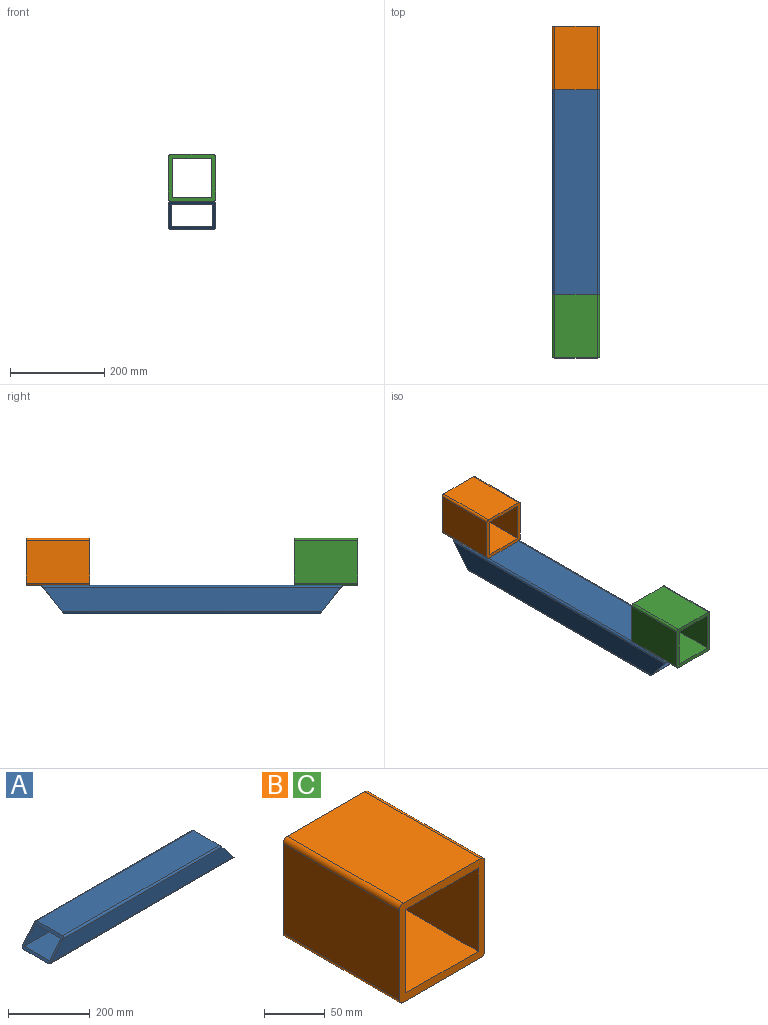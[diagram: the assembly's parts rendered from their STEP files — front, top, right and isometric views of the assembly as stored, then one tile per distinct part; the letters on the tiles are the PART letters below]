
ASSEMBLY  parts=3 mates=2
PART A: 14 faces, bbox 640x100x60 mm
  f0: cylinder r=5mm len=550.92mm, axis (-1,0,0), area 4286.5mm2, adj f1,f11,f12,f13
  f1: plane 631.9x50mm, normal (0,-1,0), area 29570.6mm2, adj f0,f2,f12,f13
  f2: cylinder r=5mm len=640mm, axis (-1,0,0), area 5003.4mm2, adj f1,f3,f12,f13
  f3: plane 640x90mm, normal (0,0,-1), area 57600mm2, adj f2,f4,f12,f13
  f4: cylinder r=5mm len=640mm, axis (-1,0,0), area 5003.4mm2, adj f3,f5,f12,f13
  f5: plane 631.9x50mm, normal (0,1,0), area 29570.6mm2, adj f4,f6,f12,f13
  f6: cylinder r=5mm len=550.92mm, axis (-1,0,0), area 4286.5mm2, adj f5,f11,f12,f13
  f7: plane 630.28x48mm, normal (0,1,0), area 28387.8mm2, adj f8,f10,f12,f13
  f8: plane 552.54x88mm, normal (0,0,-1), area 48623.8mm2, adj f7,f9,f12,f13
  f9: plane 630.28x48mm, normal (0,-1,0), area 28387.8mm2, adj f8,f10,f12,f13
  f10: plane 630.28x88mm, normal (0,0,1), area 55464.9mm2, adj f7,f9,f12,f13
  f11: plane 542.83x90mm, normal (0,0,1), area 48854.3mm2, adj f0,f6,f12,f13
  f12: plane 100x60mm, normal (-0.78,0,0.63), area 2257.7mm2, adj f0,f1,f2,f3,f4,f5,f6,f7
  f13: plane 100x60mm, normal (0.78,0,0.63), area 2257.7mm2, adj f0,f1,f2,f3,f4,f5,f6,f7
PART B: 14 faces, bbox 100x135x100 mm
  f0: cylinder r=5mm len=135mm, axis (0,1,0), area 1060.3mm2, adj f1,f11,f12,f13
  f1: plane 135x90mm, normal (-1,0,0), area 12150mm2, adj f0,f2,f12,f13
  f2: cylinder r=5mm len=135mm, axis (0,1,0), area 1060.3mm2, adj f1,f3,f12,f13
  f3: plane 135x90mm, normal (0,0,-1), area 12150mm2, adj f2,f4,f12,f13
  f4: cylinder r=5mm len=135mm, axis (0,1,0), area 1060.3mm2, adj f3,f5,f12,f13
  f5: plane 135x90mm, normal (1,0,0), area 12150mm2, adj f4,f6,f12,f13
  f6: cylinder r=5mm len=135mm, axis (0,1,0), area 1060.3mm2, adj f5,f11,f12,f13
  f7: plane 135x84mm, normal (1,0,0), area 11340mm2, adj f8,f10,f12,f13
  f8: plane 135x84mm, normal (0,0,-1), area 11340mm2, adj f7,f9,f12,f13
  f9: plane 135x84mm, normal (-1,0,0), area 11340mm2, adj f8,f10,f12,f13
  f10: plane 135x84mm, normal (0,0,1), area 11340mm2, adj f7,f9,f12,f13
  f11: plane 135x90mm, normal (0,0,1), area 12150mm2, adj f0,f6,f12,f13
  f12: plane 100x100mm, normal (0,-1,0), area 2922.5mm2, adj f0,f1,f2,f3,f4,f5,f6,f7
  f13: plane 100x100mm, normal (0,1,0), area 2922.5mm2, adj f0,f1,f2,f3,f4,f5,f6,f7
PART C: same geometry as B
PLACE A rot(axis=(0.71,0.71,0),180deg) t=(162.31,697.77,-186.03)mm
PLACE B rot(axis=(0,0,1),180deg) t=(162.31,1235.27,-186.03)mm
PLACE C t=(62.31,800.27,-186.03)mm
MATE fastened A.f3 <-> C.f3  axis (0,0,1) through (112.31,697.77,-186.03)mm
MATE fastened A.f3 <-> B.f3  axis (0,0,1) through (112.31,1337.77,-186.03)mm
